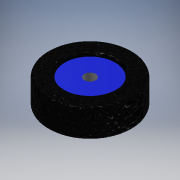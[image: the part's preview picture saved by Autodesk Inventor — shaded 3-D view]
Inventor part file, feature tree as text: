
AUTODESK INVENTOR PART (.ipt)
format: ipt  version: 2017 (Build 210142000, 142)  size: 166,912 bytes
history: native  units: mm
features: revolve x1, sketch x1
ambient origin geometry x8: Origin, YZ Plane, XZ Plane, XY Plane, X Axis, Y Axis, Z Axis, Center Point
bodies: Solid1 (feature_tree)
feature tree (2):
  revolve  "Revolution1"  [1 undecoded]
  sketch  "Sketch1"  dims[d0=560.317934mm d1=40.0mm d2=30.0mm d3=30.0mm d4=150.0mm d5=2.0mm d6=5.0mm d7=20.0mm d8=90.0deg]
note: 1 required parameter value undecoded (feature->parameter linkage not recoverable at this tier; creation-order binding heuristic only, values carry confidence <= 0.55)
